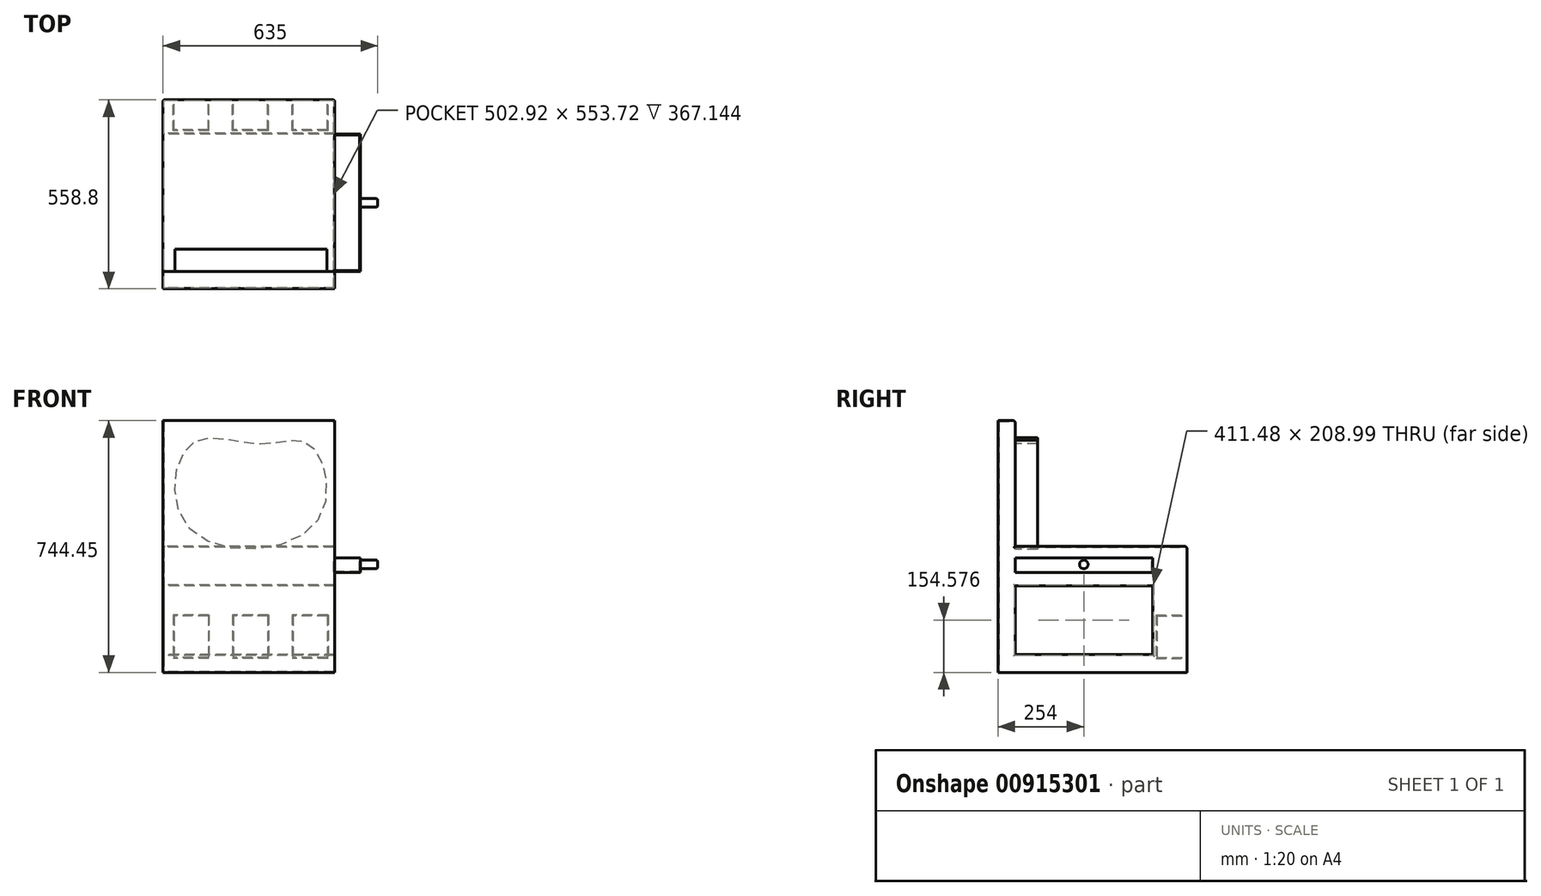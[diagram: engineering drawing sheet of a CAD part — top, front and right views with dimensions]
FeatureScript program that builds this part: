
annotation { "Feature Type Name" : "Feature", "Feature Type Description" : "" }
export const myFeature = defineFeature(function(context is Context, id is Id, definition is map)
    precondition{}
    {
        {
            var Q0;
            Q0=qCreatedBy(makeId("Right.planeOp"),FACE);
            var sketch = newSketch(context, id + "F0", { "sketchPlane" : qUnion([Q0])});
            skLineSegment(sketch, "E0.bottom", {"start": v(-457.2, 487.92) * mm, "end": v(-406.4, 487.92) * mm});
            skLineSegment(sketch, "E0.top", {"start": v(-457.2, -256.53) * mm, "end": v(-406.4, -256.53) * mm});
            skLineSegment(sketch, "E0.left", {"start": v(-457.2, 487.92) * mm, "end": v(-457.2, -256.53) * mm});
            skLineSegment(sketch, "E0.right", {"start": v(-406.4, 487.92) * mm, "end": v(-406.4, -203.9) * mm});
            skLineSegment(sketch, "E1", {"start": v(-406.4, 115.7) * mm, "end": v(101.6, 115.7) * mm});
            skLineSegment(sketch, "E2", {"start": v(101.6, 115.7) * mm, "end": v(101.6, -256.53) * mm});
            skLineSegment(sketch, "E3", {"start": v(-406.4, 0) * mm, "end": v(0, 0) * mm});
            skLineSegment(sketch, "E4", {"start": v(0, 0) * mm, "end": v(0, -203.9) * mm});
            skLineSegment(sketch, "E5", {"start": v(0, -256.53) * mm, "end": v(101.6, -256.53) * mm});
            skLineSegment(sketch, "E6", {"start": v(0, -203.9) * mm, "end": v(-406.4, -203.9) * mm});
            skLineSegment(sketch, "E7", {"start": v(0, -256.53) * mm, "end": v(-406.4, -256.53) * mm});
            skSolve(sketch);
        }
        {
            var Q0;
            Q0 = qSketchRegion(id + "F0", true);
            extrude(context, id + "F1", {"entities" : qUnion([Q0]), "depth" : 508 * mm, "offsetDistance" : 25.4 * mm});
        }
        {
            var Q0;
            {var subQ0=sQuery(id+"F0.wireOp",EDGE,"E0.right");Q0=makeQuery(id+"F1.opExtrude","SWEPT_FACE",FACE,{"disambiguationData":[OSD([subQ0]),TDD([makeQuery(id+"F0.imprint","IMPRINT",EDGE,{"disambiguationData":[TD([[makeQuery(id+"F0.imprint","INTERSECT",VERTEX,{"derivedFrom":[sQuery(id+"F0.wireOp",EDGE,"E0.bottom"),subQ0]}),-1.0]])],"derivedFrom":subQ0})])]});}
            var sketch = newSketch(context, id + "F2", { "sketchPlane" : qUnion([Q0])});
            skFitSpline(sketch, "E8", {"points": [v(-288.57, 419.7) * mm, v(-434.45, 417.18) * mm, v(-451.36, 184.19) * mm, v(-81.02, 166.05) * mm, v(-84.5, 419.98) * mm, v(-288.57, 419.7) * mm]});
            skSolve(sketch);
        }
        {
            var Q0;
            Q0 = qSketchRegion(id + "F2", true);
            extrude(context, id + "F3", {"entities" : qUnion([Q0]), "depth" : 66.04 * mm, "offsetDistance" : 25.4 * mm});
        }
        {
            var Q0;
            Q0=makeQuery(id+"F1.opExtrude","SWEPT_FACE",FACE,{"disambiguationData":[OSD([sQuery(id+"F0.wireOp",EDGE,"E2")])]});
            var sketch = newSketch(context, id + "F4", { "sketchPlane" : qUnion([Q0])});
            skLineSegment(sketch, "E9.bottom", {"start": v(-485.72, -89.03) * mm, "end": v(-384.12, -89.03) * mm});
            skLineSegment(sketch, "E9.top", {"start": v(-485.72, -212.85) * mm, "end": v(-384.12, -212.85) * mm});
            skLineSegment(sketch, "E9.left", {"start": v(-485.72, -89.03) * mm, "end": v(-485.72, -212.85) * mm});
            skLineSegment(sketch, "E9.right", {"start": v(-384.12, -89.03) * mm, "end": v(-384.12, -212.85) * mm});
            skLineSegment(sketch, "E10.bottom", {"start": v(-309.76, -89.03) * mm, "end": v(-208.16, -89.03) * mm});
            skLineSegment(sketch, "E10.top", {"start": v(-309.76, -212.85) * mm, "end": v(-208.16, -212.85) * mm});
            skLineSegment(sketch, "E10.left", {"start": v(-309.76, -89.03) * mm, "end": v(-309.76, -212.85) * mm});
            skLineSegment(sketch, "E10.right", {"start": v(-208.16, -89.03) * mm, "end": v(-208.16, -212.85) * mm});
            skLineSegment(sketch, "E11.bottom", {"start": v(-133.78, -89.03) * mm, "end": v(-32.18, -89.03) * mm});
            skLineSegment(sketch, "E11.top", {"start": v(-133.78, -212.85) * mm, "end": v(-32.18, -212.85) * mm});
            skLineSegment(sketch, "E11.left", {"start": v(-133.78, -89.03) * mm, "end": v(-133.78, -212.85) * mm});
            skLineSegment(sketch, "E11.right", {"start": v(-32.18, -89.03) * mm, "end": v(-32.18, -212.85) * mm});
            skSolve(sketch);
        }
        {
            var Q0;
            Q0=makeQuery(id+"F4.imprint","IMPRINT",FACE,{"disambiguationData":[TD([[makeQuery(id+"F4.imprint","IMPRINT",EDGE,{"derivedFrom":sQuery(id+"F4.wireOp",EDGE,"E9.bottom")}),-1.0]])]});
            var Q1;
            Q1=makeQuery(id+"F4.imprint","IMPRINT",FACE,{"disambiguationData":[TD([[makeQuery(id+"F4.imprint","IMPRINT",EDGE,{"derivedFrom":sQuery(id+"F4.wireOp",EDGE,"E10.bottom")}),-1.0]])]});
            var Q2;
            Q2=makeQuery(id+"F4.imprint","IMPRINT",FACE,{"disambiguationData":[TD([[makeQuery(id+"F4.imprint","IMPRINT",EDGE,{"derivedFrom":sQuery(id+"F4.wireOp",EDGE,"E11.bottom")}),-1.0]])]});
            extrude(context, id + "F5", {"entities" : qUnion([Q0, Q1, Q2]), "operationType" : NewBodyOperationType.REMOVE, "oppositeDirection" : true, "depth" : 88.9 * mm, "offsetDistance" : 25.4 * mm});
        }
        {
            var Q0;
            Q0=makeQuery(id+"F1.opExtrude","CAP_FACE",FACE,{"disambiguationData":[OSD([sQuery(id+"F0.wireOp",EDGE,"E0.bottom"),sQuery(id+"F0.wireOp",EDGE,"E0.top"),sQuery(id+"F0.wireOp",EDGE,"E0.left"),sQuery(id+"F0.wireOp",EDGE,"E0.right"),sQuery(id+"F0.wireOp",EDGE,"E1"),sQuery(id+"F0.wireOp",EDGE,"E2"),sQuery(id+"F0.wireOp",EDGE,"E3"),sQuery(id+"F0.wireOp",EDGE,"E4"),sQuery(id+"F0.wireOp",EDGE,"E5"),sQuery(id+"F0.wireOp",EDGE,"E6"),sQuery(id+"F0.wireOp",EDGE,"E7")])],"isStart":false});
            var sketch = newSketch(context, id + "F6", { "sketchPlane" : qUnion([Q0])});
            skLineSegment(sketch, "E12.bottom", {"start": v(-406.4, 39.24) * mm, "end": v(0, 39.24) * mm});
            skLineSegment(sketch, "E12.top", {"start": v(-406.4, 82.42) * mm, "end": v(0, 82.42) * mm});
            skLineSegment(sketch, "E12.left", {"start": v(-406.4, 39.24) * mm, "end": v(-406.4, 82.42) * mm});
            skLineSegment(sketch, "E12.right", {"start": v(0, 39.24) * mm, "end": v(0, 82.42) * mm});
            skSolve(sketch);
        }
        {
            var Q0;
            Q0=makeQuery(id+"F6.imprint","IMPRINT",FACE,{"disambiguationData":[TD([[makeQuery(id+"F6.imprint","IMPRINT",EDGE,{"derivedFrom":sQuery(id+"F6.wireOp",EDGE,"E12.bottom")}),1.0]])]});
            extrude(context, id + "F7", {"entities" : qUnion([Q0]), "operationType" : NewBodyOperationType.ADD, "depth" : 76.2 * mm, "offsetDistance" : 25.4 * mm});
        }
        {
            var Q0;
            Q0=makeQuery(id+"F7.opExtrude","SWEPT_FACE",FACE,{"disambiguationData":[OSD([sQuery(id+"F6.wireOp",EDGE,"E12.top")])]});
            shell(context, id + "F8", {"entities" : qUnion([Q0]), "thickness" : 2.54 * mm});
        }
        {
            var Q0;
            Q0=makeQuery(id+"F7.opExtrude","CAP_FACE",FACE,{"disambiguationData":[OSD([sQuery(id+"F6.wireOp",EDGE,"E12.bottom"),sQuery(id+"F6.wireOp",EDGE,"E12.top"),sQuery(id+"F6.wireOp",EDGE,"E12.left"),sQuery(id+"F6.wireOp",EDGE,"E12.right")])],"isStart":false});
            var sketch = newSketch(context, id + "F9", { "sketchPlane" : qUnion([Q0])});
            skCircle(sketch, "E13", {"center": v(-203.2, 62.64) * mm, "radius": 12.7 * mm});
            skSolve(sketch);
        }
        {
            var Q0;
            Q0=makeQuery(id+"F9.imprint","IMPRINT",FACE,{"disambiguationData":[TD([[makeQuery(id+"F9.imprint","IMPRINT",EDGE,{"derivedFrom":sQuery(id+"F9.wireOp",EDGE,"E13")}),1.0]])]});
            extrude(context, id + "F10", {"entities" : qUnion([Q0]), "operationType" : NewBodyOperationType.ADD, "depth" : 50.8 * mm, "offsetDistance" : 25.4 * mm});
        }
        {
            var Q0;
            Q0=makeQuery(id+"F1.opExtrude","CAP_EDGE",EDGE,{"disambiguationData":[OSD([sQuery(id+"F0.wireOp",EDGE,"E2")])],"isStart":false});
            var Q1;
            Q1=makeQuery(id+"F1.opExtrude","CAP_EDGE",EDGE,{"disambiguationData":[OSD([sQuery(id+"F0.wireOp",EDGE,"E2")])],"isStart":true});
            var Q2;
            Q2=makeQuery(id+"F1.opExtrude","SWEPT_EDGE",EDGE,{"disambiguationData":[OSD([sQuery(id+"F0.wireOp",EDGE,"E1"),sQuery(id+"F0.wireOp",EDGE,"E2")])]});
            var Q3;
            Q3=makeQuery(id+"F1.opExtrude","CAP_EDGE",EDGE,{"disambiguationData":[OSD([sQuery(id+"F0.wireOp",EDGE,"E1")])],"isStart":true});
            var Q4;
            {var subQ0=sQuery(id+"F0.wireOp",EDGE,"E0.right");Q4=makeQuery(id+"F1.opExtrude","CAP_EDGE",EDGE,{"disambiguationData":[OSD([subQ0]),TDD([makeQuery(id+"F0.imprint","IMPRINT",EDGE,{"disambiguationData":[TD([[makeQuery(id+"F0.imprint","INTERSECT",VERTEX,{"derivedFrom":[sQuery(id+"F0.wireOp",EDGE,"E0.bottom"),subQ0]}),-1.0]])],"derivedFrom":subQ0})])],"isStart":true});}
            var Q5;
            Q5=makeQuery(id+"F1.opExtrude","SWEPT_EDGE",EDGE,{"disambiguationData":[OSD([sQuery(id+"F0.wireOp",EDGE,"E0.bottom"),sQuery(id+"F0.wireOp",EDGE,"E0.right")])]});
            var Q6;
            {var subQ0=sQuery(id+"F0.wireOp",EDGE,"E0.right");Q6=makeQuery(id+"F1.opExtrude","CAP_EDGE",EDGE,{"disambiguationData":[OSD([subQ0]),TDD([makeQuery(id+"F0.imprint","IMPRINT",EDGE,{"disambiguationData":[TD([[makeQuery(id+"F0.imprint","INTERSECT",VERTEX,{"derivedFrom":[sQuery(id+"F0.wireOp",EDGE,"E0.bottom"),subQ0]}),-1.0]])],"derivedFrom":subQ0})])],"isStart":false});}
            var Q7;
            Q7=makeQuery(id+"F1.opExtrude","CAP_EDGE",EDGE,{"disambiguationData":[OSD([sQuery(id+"F0.wireOp",EDGE,"E1")])],"isStart":false});
            var Q8;
            Q8=makeQuery(id+"F10.opExtrude","SWEPT_FACE",FACE,{"disambiguationData":[OSD([sQuery(id+"F9.wireOp",EDGE,"E13")])]});
            var Q9;
            {var subQ0=sQuery(id+"F0.wireOp",EDGE,"E0.right");Q9=makeQuery(id+"F1.opExtrude","CAP_EDGE",EDGE,{"disambiguationData":[OSD([subQ0]),TDD([makeQuery(id+"F0.imprint","IMPRINT",EDGE,{"disambiguationData":[TD([[makeQuery(id+"F0.imprint","INTERSECT",VERTEX,{"derivedFrom":[subQ0,sQuery(id+"F0.wireOp",EDGE,"E6")]}),1.0]])],"derivedFrom":subQ0})])],"isStart":true});}
            var Q10;
            Q10=makeQuery(id+"F1.opExtrude","CAP_EDGE",EDGE,{"disambiguationData":[OSD([sQuery(id+"F0.wireOp",EDGE,"E3")])],"isStart":true});
            var Q11;
            Q11=makeQuery(id+"F1.opExtrude","CAP_EDGE",EDGE,{"disambiguationData":[OSD([sQuery(id+"F0.wireOp",EDGE,"E4")])],"isStart":true});
            var Q12;
            Q12=makeQuery(id+"F1.opExtrude","CAP_EDGE",EDGE,{"disambiguationData":[OSD([sQuery(id+"F0.wireOp",EDGE,"E6")])],"isStart":true});
            fillet(context, id + "F11", {"entities" : qUnion([Q0, Q1, Q2, Q3, Q4, Q5, Q6, Q7, Q8, Q9, Q10, Q11, Q12]), "radius" : 5.08 * mm, "tangentPropagation" : true, "allowEdgeOverflow" : false});
        }
    });
